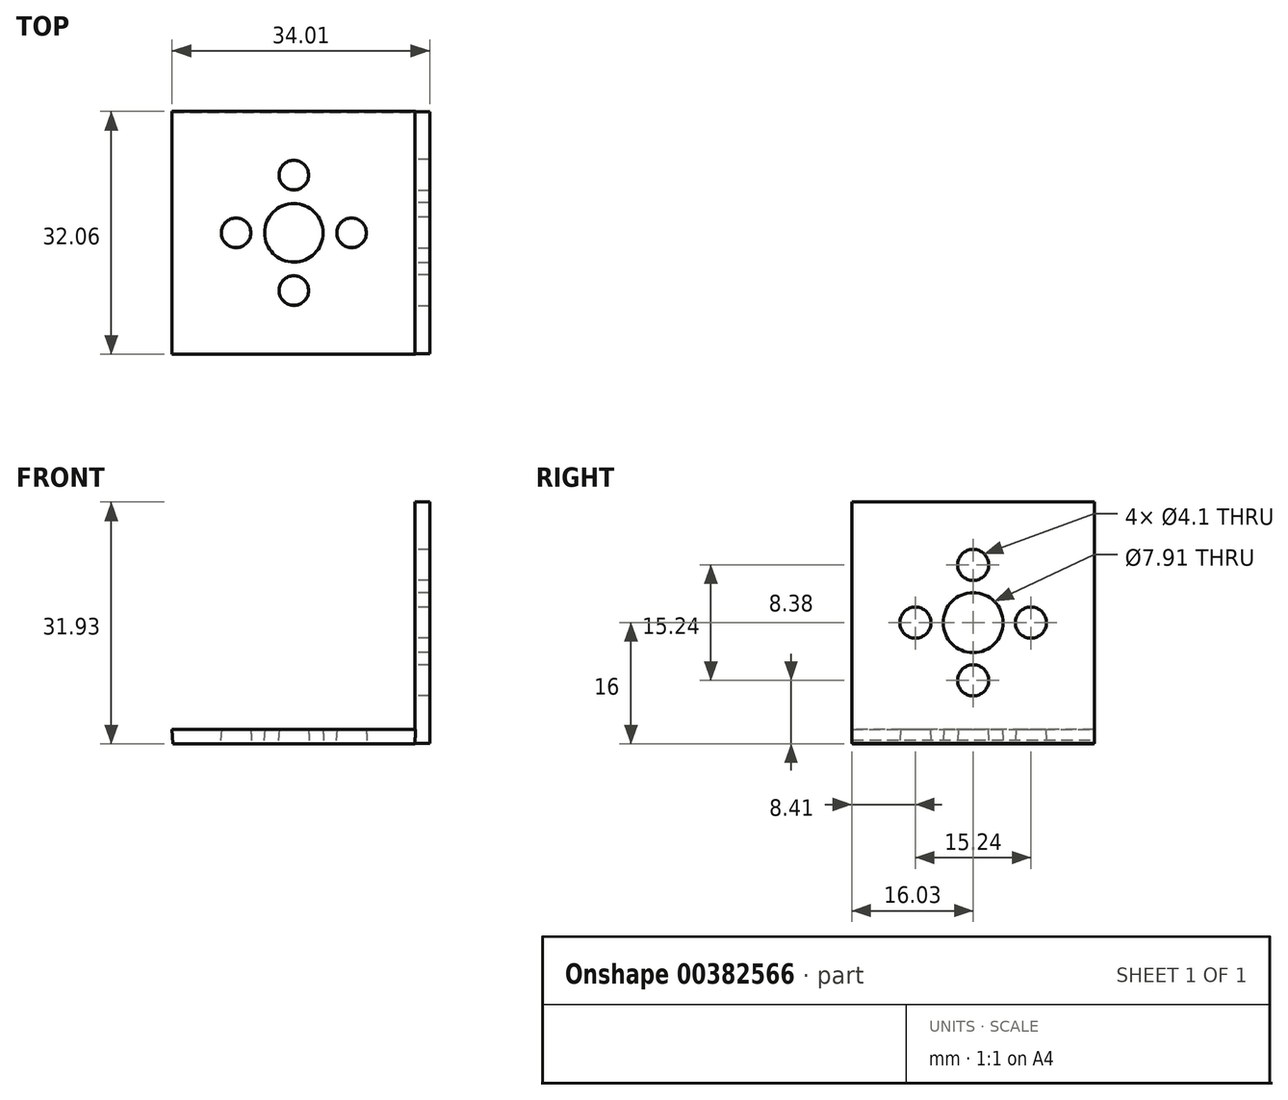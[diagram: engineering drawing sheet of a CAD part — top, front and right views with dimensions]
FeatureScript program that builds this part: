
annotation { "Feature Type Name" : "Feature", "Feature Type Description" : "" }
export const myFeature = defineFeature(function(context is Context, id is Id, definition is map)
    precondition{}
    {
        {
            var Q0;
            Q0=qCreatedBy(makeId("Top.planeOp"),FACE);
            cPlane(context, id + "F0", {"entities" : qUnion([Q0]), "cplaneType" : CPlaneType.OFFSET, "offset" : 16 * mm, "oppositeDirection" : true, "width" : 152.4 * mm, "height" : 152.4 * mm});
        }
        {
            var Q0;
            Q0=qCreatedBy(id+"F0.planeOp",FACE);
            var sketch = newSketch(context, id + "F1", { "sketchPlane" : qUnion([Q0])});
            skLineSegment(sketch, "E0.bottom", {"start": v(15.98, -15.93) * mm, "end": v(-15.97, -15.93) * mm});
            skLineSegment(sketch, "E0.top", {"start": v(15.98, 15.93) * mm, "end": v(-15.97, 15.93) * mm});
            skLineSegment(sketch, "E0.left", {"start": v(15.98, -15.93) * mm, "end": v(15.98, 15.93) * mm});
            skLineSegment(sketch, "E0.right", {"start": v(-15.97, -15.93) * mm, "end": v(-15.97, 15.93) * mm});
            skPoint(sketch, "E0.middle", {"position": v(0, 0) * mm});
            skCircle(sketch, "E1", {"center": v(0, 0) * mm, "radius": 3.96 * mm});
            skCircle(sketch, "E2", {"center": v(0, 7.62) * mm, "radius": 2.05 * mm});
            skCircle(sketch, "E3", {"center": v(-7.62, 0) * mm, "radius": 2.05 * mm});
            skCircle(sketch, "E4", {"center": v(0, -7.62) * mm, "radius": 2.05 * mm});
            skCircle(sketch, "E5", {"center": v(7.62, 0) * mm, "radius": 2.05 * mm});
            skSolve(sketch);
        }
        {
            var Q0;
            Q0=qCreatedBy(makeId("Right.planeOp"),FACE);
            cPlane(context, id + "F2", {"entities" : qUnion([Q0]), "cplaneType" : CPlaneType.OFFSET, "offset" : 16 * mm, "width" : 152.4 * mm, "height" : 152.4 * mm});
        }
        {
            var Q0;
            Q0=qCreatedBy(id+"F2.planeOp",FACE);
            var sketch = newSketch(context, id + "F3", { "sketchPlane" : qUnion([Q0])});
            skLineSegment(sketch, "E6.bottom", {"start": v(15.98, -15.93) * mm, "end": v(-15.97, -15.93) * mm});
            skLineSegment(sketch, "E6.top", {"start": v(15.98, 15.93) * mm, "end": v(-15.97, 15.93) * mm});
            skLineSegment(sketch, "E6.left", {"start": v(15.98, -15.93) * mm, "end": v(15.98, 15.93) * mm});
            skLineSegment(sketch, "E6.right", {"start": v(-15.97, -15.93) * mm, "end": v(-15.97, 15.93) * mm});
            skPoint(sketch, "E6.middle", {"position": v(0, 0) * mm});
            skCircle(sketch, "E7", {"center": v(0, 0) * mm, "radius": 3.96 * mm});
            skCircle(sketch, "E8", {"center": v(0, 7.62) * mm, "radius": 2.05 * mm});
            skCircle(sketch, "E9", {"center": v(-7.62, 0) * mm, "radius": 2.05 * mm});
            skCircle(sketch, "E10", {"center": v(0, -7.62) * mm, "radius": 2.05 * mm});
            skCircle(sketch, "E11", {"center": v(7.62, 0) * mm, "radius": 2.05 * mm});
            skSolve(sketch);
        }
        {
            var Q0;
            Q0=makeQuery(id+"F3.imprint","IMPRINT",FACE,{"disambiguationData":[TD([[makeQuery(id+"F3.imprint","IMPRINT",EDGE,{"derivedFrom":sQuery(id+"F3.wireOp",EDGE,"E6.bottom")}),-1.0]])]});
            extrude(context, id + "F4", {"entities" : qUnion([Q0]), "depth" : 1.93 * mm});
        }
        {
            var Q0;
            Q0=makeQuery(id+"F1.imprint","IMPRINT",FACE,{"disambiguationData":[TD([[makeQuery(id+"F1.imprint","IMPRINT",EDGE,{"derivedFrom":sQuery(id+"F1.wireOp",EDGE,"E0.bottom")}),-1.0]])]});
            extrude(context, id + "F5", {"entities" : qUnion([Q0]), "operationType" : NewBodyOperationType.ADD, "depth" : 1.93 * mm, "hasDraft" : true, "draftAngle" : 3 * degree});
        }
    });
